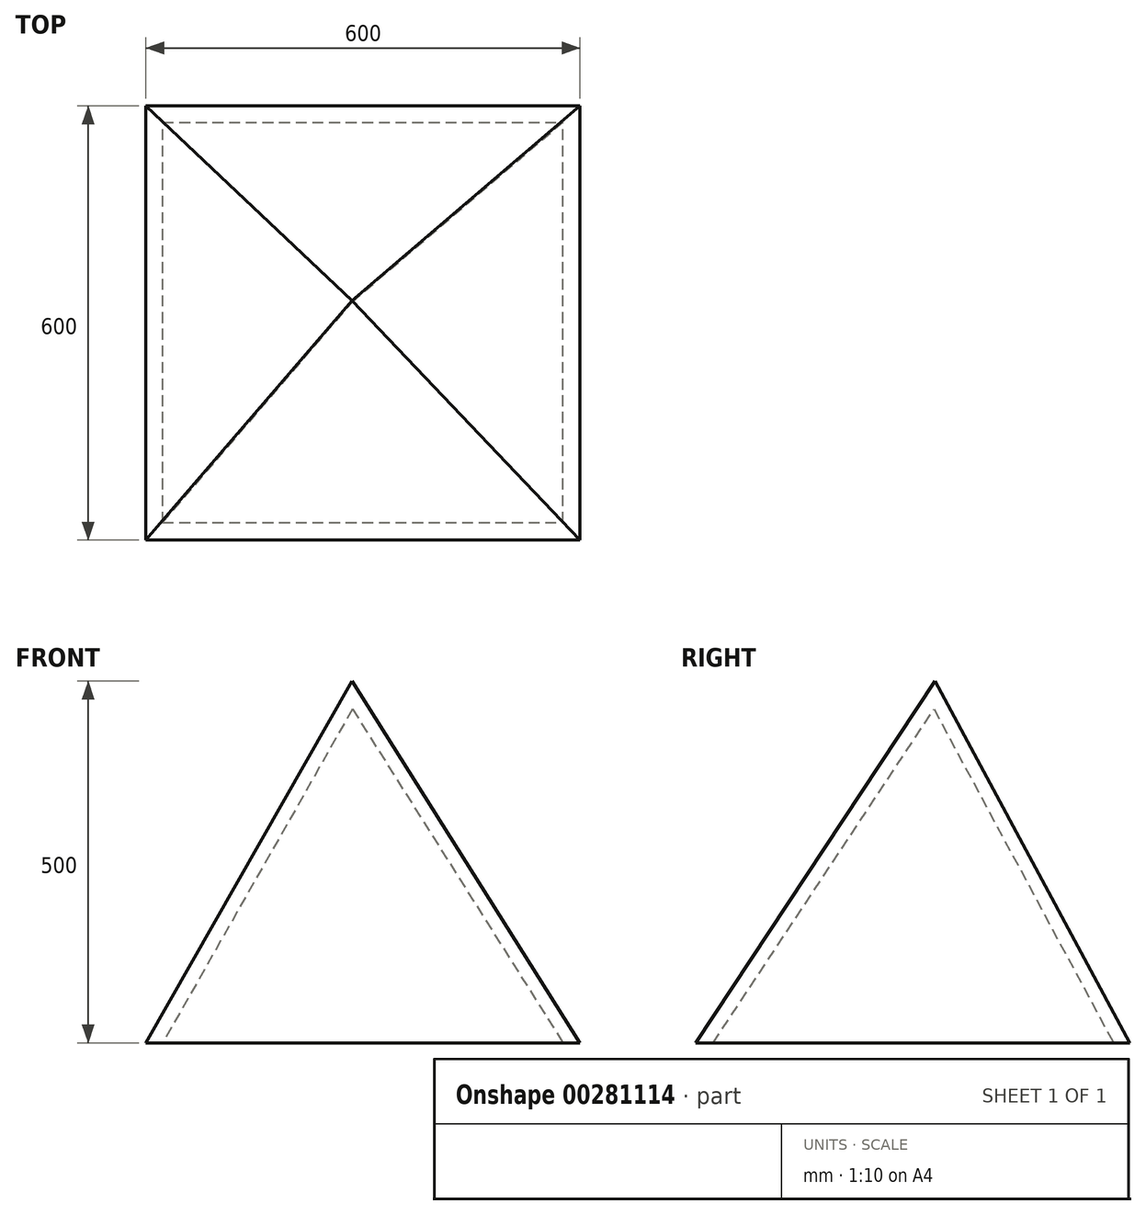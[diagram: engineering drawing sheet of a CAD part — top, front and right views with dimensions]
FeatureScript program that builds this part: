
annotation { "Feature Type Name" : "Feature", "Feature Type Description" : "" }
export const myFeature = defineFeature(function(context is Context, id is Id, definition is map)
    precondition{}
    {
        {
            var Q0;
            Q0=qCreatedBy(makeId("Top.planeOp"),FACE);
            var sketch = newSketch(context, id + "F0", { "sketchPlane" : qUnion([Q0])});
            skLineSegment(sketch, "E0.bottom", {"start": v(0, 0) * mm, "end": v(600, 0) * mm});
            skLineSegment(sketch, "E0.top", {"start": v(0, 600) * mm, "end": v(600, 600) * mm});
            skLineSegment(sketch, "E0.left", {"start": v(0, 0) * mm, "end": v(0, 600) * mm});
            skLineSegment(sketch, "E0.right", {"start": v(600, 0) * mm, "end": v(600, 600) * mm});
            skSolve(sketch);
        }
        {
            var Q0;
            Q0=makeQuery(id+"F0.imprint","IMPRINT",FACE,{"disambiguationData":[TD([[makeQuery(id+"F0.imprint","IMPRINT",EDGE,{"derivedFrom":sQuery(id+"F0.wireOp",EDGE,"E0.bottom")}),1.0]])]});
            cPlane(context, id + "F1", {"entities" : qUnion([Q0]), "cplaneType" : CPlaneType.OFFSET, "offset" : 500 * mm, "width" : 150 * mm, "height" : 150 * mm});
        }
        {
            var Q0;
            Q0=qCreatedBy(id+"F1.planeOp",FACE);
            var sketch = newSketch(context, id + "F2", { "sketchPlane" : qUnion([Q0])});
            skPoint(sketch, "E1", {"position": v(284.55, 330.9) * mm});
            skPoint(sketch, "E2", {"position": v(284.55, 661.48) * mm});
            skPoint(sketch, "E3", {"position": v(-58.43, 330.9) * mm});
            skSolve(sketch);
        }
        {
            var Q0;
            Q0=sQuery(id+"F2.wireOp",VERTEX,"E1");
            var Q1;
            Q1=makeQuery(id+"F0.imprint","IMPRINT",FACE,{"disambiguationData":[TD([[makeQuery(id+"F0.imprint","IMPRINT",EDGE,{"derivedFrom":sQuery(id+"F0.wireOp",EDGE,"E0.bottom")}),1.0]])]});
            loft(context, id + "F3", {"sheetProfilesArray" : [{ "sheetProfileEntities" : qUnion([Q0]) }, { "sheetProfileEntities" : qUnion([Q1]) }]});
        }
        {
            var Q0;
            Q0=makeQuery(id+"F3.opLoft","CAP_FACE",FACE,{"disambiguationData":[OSD([makeQuery(id+"F0.imprint","IMPRINT",FACE,{"disambiguationData":[TD([[makeQuery(id+"F0.imprint","IMPRINT",EDGE,{"derivedFrom":sQuery(id+"F0.wireOp",EDGE,"E0.bottom")}),1.0]])]})])],"isStart":true});
            shell(context, id + "F4", {"entities" : qUnion([Q0]), "thickness" : 20 * mm});
        }
    });
